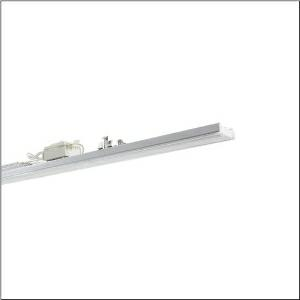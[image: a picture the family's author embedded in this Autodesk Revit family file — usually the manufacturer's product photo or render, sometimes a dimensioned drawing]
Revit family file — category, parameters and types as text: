
# Revit family: licross_r__11_recessed_mo_51tl14dv4exg_cd34
name_source: partatom
category: Lighting Fixtures
units: mm (PartAtom-declared; Revit-internal decimal feet)

## family parameters
Cut with Voids When Loaded = No
Host = Face
Light Source = No
Part Type = Normal
Room Calculation Point = No
Round Connector Dimension = Use Diameter
Shared = No

## types (1)
- --- (1 x LED, 14140 lm, 84.1 W, 4000K)
    Apparent Load = 84 VA
    CIE Flux Codes = 56 84 97 100 100
    Color Rendering = 80
    Color Temperature = 4000K
    Default Elevation = 1800 mm
    Description = Licross® 11 Recessed MO, luminaire insert, of sheet steel, coil coated, white, length: 2.250mm, width: 66mm, height: 67mm, LED rated luminous flux: 14.140lm, light colour: 840, control gear: DALI 2, with plug, 5-pole, with phase selection, mains connection: 220..240V, AC, 50/60Hz, rated input power: 84W, halogen-free wiring, primary light control with lens, of plastic, primary optical cover: cover, of PMMA, light emission: direct distribution, primary light characteristic: asymmetric, protection rating (complete): IP40, insulation class (complete): insulation class I (protective earthing), certification: CE, ENEC, VDE, UKCA, protection symbol: D if used in an environment without relevant dust loads with corresponding accessories, impact resistance: IK06, permissible ambient temperature for indoor applications: -25..+35°C, corresponds to IFS (International Featured Standards) requirements for safety and quality in the food industry, reducing of maximum allowable ambient temperature of 5°C with ceiling mounting, LABS conformity tested according to VDMA 24364:2018-05, packaging unit: 1 piece
    Height = 58 mm
    Lamp = 1 x LED
    Lamp Light Flux = 14140 lm
    Lamp Power = 84.1 W
    Lamp count = 1
    Length = 2250 mm
    Luminous efficacy = 168 lm/W
    Manufacturer = Siteco
    ModVariant = No
    Model = 51TL14DV4EXG
    Mounting Place = Ceiling
    Mounting Type = Pendant
    Number of Poles = 1
    OnlyDefault = Yes
    Power Factor = 1
    Product Name = Licross® 11 Recessed MO
    Product group = luminaire insert
    ProductGroupID = 902
    Protection Class = Protection class I
    Protection Degree = IP 40
    RLX_Detail_Level = 1
    RLX_Emergency_Light_Flux = 0 lm
    RLX_Emergency_Type = 0
    RLX_Emergency_Type_DB = No
    RlxData = <blob elided: 30029 chars, md5=652fa983>
    Socket = socket
    Standby Power = 0 W
    System Light Flux = 14140 lm
    System Power = 84 W
    Type Comments = factory setting: luminous flux: 100 % | dim-lin: 254 | 378 mA
    Type Image = l_1296930.jpg
    URL = http://relux.com
    VarID = @adj_100024
    Voltage = 0 V
    Weight = 0.00 kg
    Width = 66 mm

## geometry (parser evidence)
native form markers: Blend x4, Sweep x11
no freeform markers — native parametric forms only
